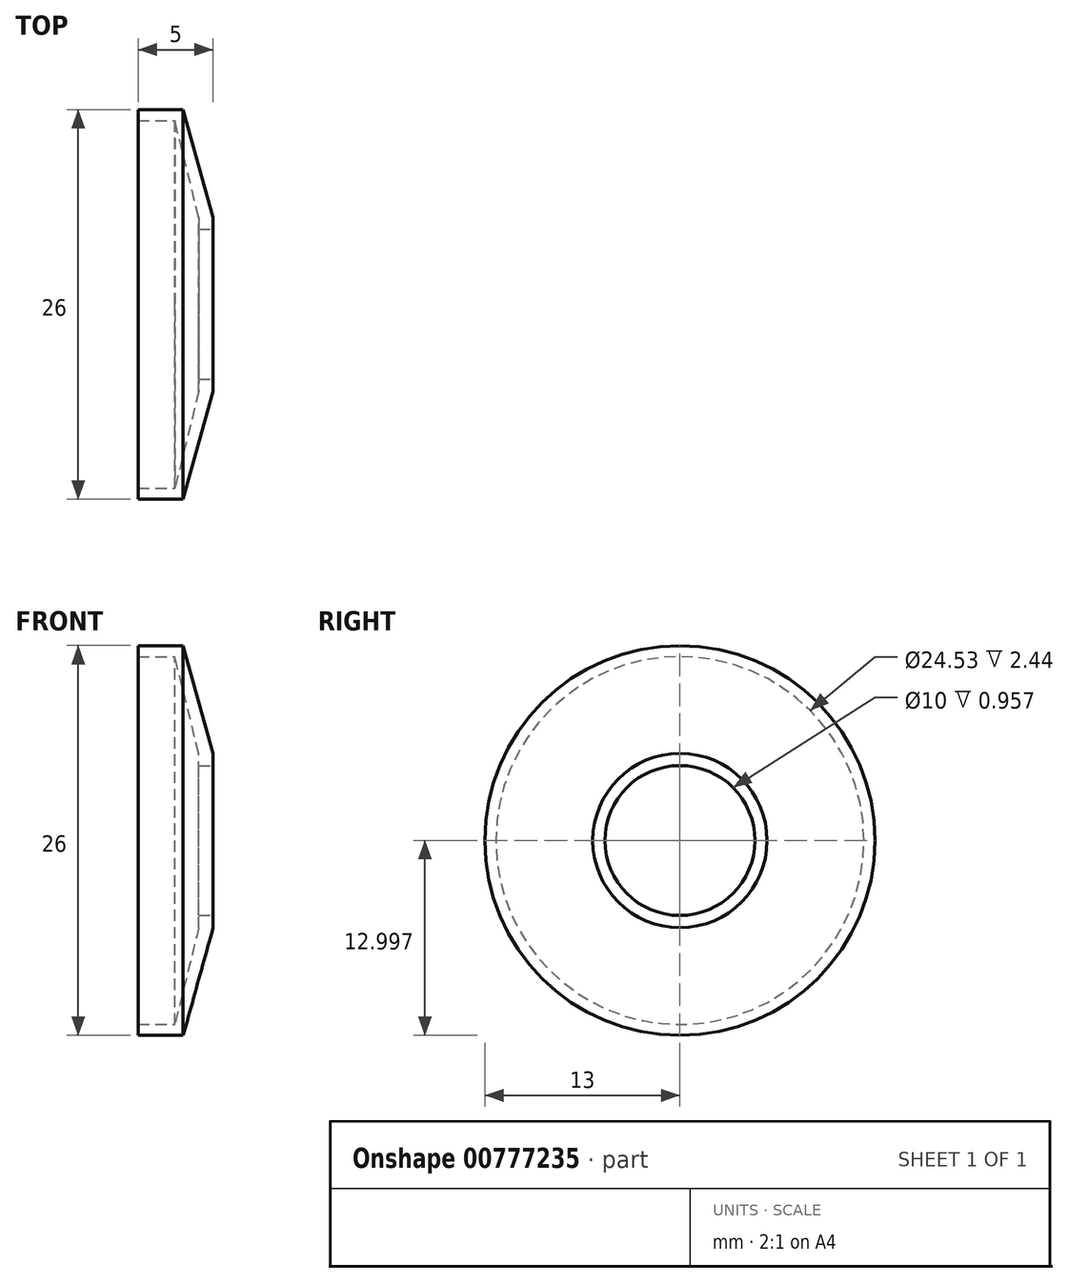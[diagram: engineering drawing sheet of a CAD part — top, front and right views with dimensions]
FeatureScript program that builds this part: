
annotation { "Feature Type Name" : "Feature", "Feature Type Description" : "" }
export const myFeature = defineFeature(function(context is Context, id is Id, definition is map)
    precondition{}
    {
        {
            var Q0;
            Q0=qCreatedBy(makeId("Front.planeOp"),FACE);
            var sketch = newSketch(context, id + "F0", { "sketchPlane" : qUnion([Q0])});
            skLineSegment(sketch, "E0.bottom", {"start": v(-5.43, 5.53) * mm, "end": v(-2.43, 5.53) * mm});
            skLineSegment(sketch, "E0.top", {"start": v(-1.38, -7.47) * mm, "end": v(-0.43, -7.47) * mm});
            skLineSegment(sketch, "E0.left", {"start": v(-5.43, 5.53) * mm, "end": v(-5.43, 4.8) * mm});
            skLineSegment(sketch, "E0.right", {"start": v(-0.43, -1.66) * mm, "end": v(-0.43, -2.47) * mm});
            skLineSegment(sketch, "E1.bottom", {"start": v(-5.43, 5.53) * mm, "end": v(-2.43, 5.53) * mm, "construction": true});
            skLineSegment(sketch, "E1.left", {"start": v(-5.43, 5.53) * mm, "end": v(-5.43, 4.8) * mm, "construction": true});
            skLineSegment(sketch, "E2.bottom", {"start": v(-0.43, -7.47) * mm, "end": v(-1.38, -7.47) * mm});
            skLineSegment(sketch, "E2.top", {"start": v(-0.43, -2.47) * mm, "end": v(-1.38, -2.47) * mm});
            skLineSegment(sketch, "E3", {"start": v(-2.43, 5.53) * mm, "end": v(-0.43, -1.66) * mm});
            skLineSegment(sketch, "E4", {"start": v(-5.43, 4.8) * mm, "end": v(-2.99, 4.8) * mm});
            skLineSegment(sketch, "E5", {"start": v(-2.99, 4.8) * mm, "end": v(-1.38, -1.66) * mm});
            skLineSegment(sketch, "E6", {"start": v(-1.38, -1.66) * mm, "end": v(-1.38, -2.47) * mm});
            skPoint(sketch, "E7.orphan", {"position": v(-0.43, 5.53) * mm});
            skSolve(sketch);
        }
        {
            var Q0;
            Q0=makeQuery(id+"F0.imprint","IMPRINT",FACE,{"disambiguationData":[TD([[makeQuery(id+"F0.imprint","IMPRINT",EDGE,{"derivedFrom":sQuery(id+"F0.wireOp",EDGE,"E0.bottom")}),-1.0]])]});
            var Q1;
            Q1=sQuery(id+"F0.wireOp",EDGE,"E2.bottom");
            revolve(context, id + "F1", {"surfaceOperationType" : NewSurfaceOperationType.NEW, "entities" : qUnion([Q0]), "axis" : qUnion([Q1]), "revolveType" : RevolveType.FULL});
        }
    });
